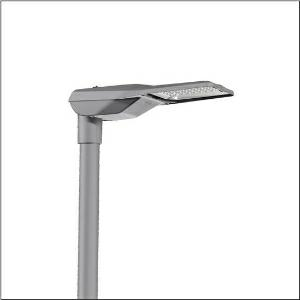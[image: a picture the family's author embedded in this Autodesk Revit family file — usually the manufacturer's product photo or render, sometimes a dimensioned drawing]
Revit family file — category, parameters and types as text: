
# Revit family: streetlight_sl_21_mini___st1_0ab_5xe2m33s08gb_a984
name_source: partatom
category: Lighting Fixtures
units: mm (PartAtom-declared; Revit-internal decimal feet)

## family parameters
Cut with Voids When Loaded = No
Host = Face
Light Source = No
Part Type = Normal
Room Calculation Point = No
Round Connector Dimension = Use Diameter
Shared = No

## types (1)
- --- (1 x LED, 5230 lm, 40.4 W, 3000K)
    Apparent Load = 40 VA
    CIE Flux Codes = 38 73 97 100 100
    Color Rendering = 70
    Color Temperature = 3000K
    Default Elevation = 1800 mm
    Description = Streetlight SL 21 mini, mast luminaire, primary light control with lens, of PMMA, primary optical cover: cover, of toughened safety glass, transparent, light distribution: ST1.0aB, light emission: direct distribution, primary light characteristic: asymmetric, installation type: side-entry, post-top, LED, High Power LED, rated luminous flux: 5.230lm, luminous efficacy: 130lm/W, light colour: 730, colour temperature: 3000K, control gear: D4i, control: flexible luminous flux parameterisation, time-dependent luminous flux control, constant luminous flux control, overheat protection, pre-setting: logarithmic dimming characteristic, mains connection: 220..240V, AC, 50/60Hz, start of lifetime: 40W, end of service life: 41W, reduction: 19W, luminaire housing, of diecast aluminium, powder-coated, SITECO metallic grey (DB 702S), corrosivity category C5 high according to DIN EN ISO 12944, please order mast flange separately, inclination adjustable: 0°, 5°, 10°, 15°, sealing non-destructively replaceable, multi-level sealing system, length: 628mm, width: 235mm, height: 110mm, mast flange for spigot size: 42mm (side-entry): 5XC10008XM4, 60/48mm (side-entry/post-top): 5XC10108XM2, 76/60mm (side-entry/post-top): 5XC10108XM1, mounting height: 4..8m, Smart Interface above, protection rating (complete): IP66, insulation class (complete): insulation class II (safety insulation), certification: CE, ENEC, ENEC+, VDE, impact resistance: IK10, permissible operating ambient temperature for outdoor applications: -40..+50°C, standard-compliant lighting for roads and squares, packaging unit: 1 piece

Light Distribution: ST1.0aB
    Height = 110 mm
    Lamp = 1 x LED
    Lamp Light Flux = 5230 lm
    Lamp Power = 40.4 W
    Lamp count = 1
    Length = 625 mm
    Luminous efficacy = 129 lm/W
    Manufacturer = Siteco
    ModVariant = No
    Model = 5XE2M33S08GB
    Number of Poles = 1
    OnlyDefault = Yes
    Power Factor = 1
    Product Name = Streetlight SL 21 mini | ST1.0aB
    Product group = mast luminaire | pylon top
    ProductGroupID = 6100
    Protection Class = Protection class II
    Protection Degree = IP 66
    RLX_Detail_Level = 1
    RLX_Emergency_Light_Flux = 0 lm
    RLX_Emergency_Type = 0
    RLX_Emergency_Type_DB = No
    RlxData = <blob elided: 26181 chars, md5=c716fd4f>
    Socket = socket
    Standby Power = 0 W
    System Light Flux = 5230 lm
    System Power = 40 W
    Type Comments = factory setting: luminous flux: 100 % | dim-lin: 254 | 812 mA
    Type Image = l_1003515.jpg
    URL = http://relux.com
    VarID = @adj_180081
    Voltage = 0 V
    Weight = 0.00 kg
    Width = 234 mm

## geometry (parser evidence)
native form markers: Blend x4, Sweep x10
no freeform markers — native parametric forms only
